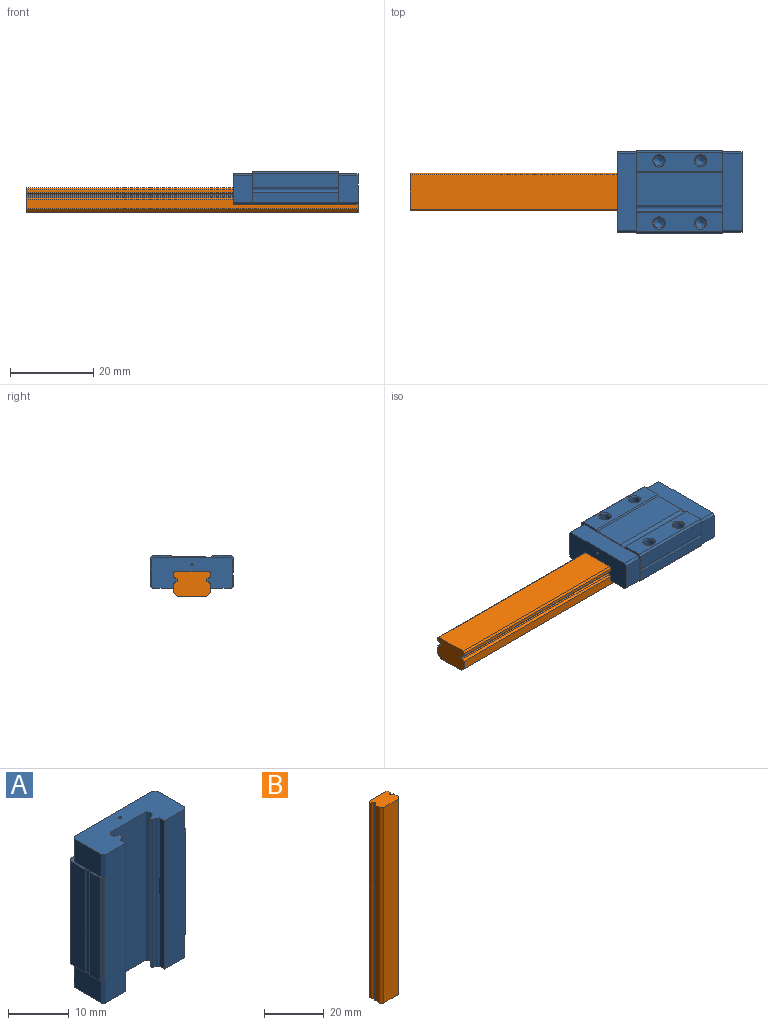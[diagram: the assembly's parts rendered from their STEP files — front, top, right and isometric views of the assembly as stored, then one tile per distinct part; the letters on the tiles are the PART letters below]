
ASSEMBLY  parts=2 mates=1
PART A: 73 faces, bbox 20x8x30 mm
  f0: plane 8x6.01mm, normal (0,0,1), area 5.3mm2, adj f2,f3,f5,f11,f15,f16,f20,f21
  f1: plane 8x6.01mm, normal (0,0,-1), area 5.3mm2, adj f2,f3,f5,f11,f15,f16,f27,f28
  f2: plane 20.8x3.47mm, normal (-1,0,0), area 72.2mm2, adj f0,f1,f16,f72
  f3: plane 20.8x2.47mm, normal (-1,0,0), area 51.4mm2, adj f0,f1,f15,f72
  f4: plane 20.8x4.5mm, normal (0,1,0), area 79.5mm2, adj f6,f7,f12,f38,f44,f68
  f5: plane 20.8x4.5mm, normal (0,1,0), area 79.5mm2, adj f0,f1,f16,f35,f41,f71
  f6: plane 13.99x8mm, normal (0,0,1), area 7.8mm2, adj f4,f10,f12,f13,f14,f17,f18,f19
  f7: plane 13.99x8mm, normal (0,0,-1), area 7.8mm2, adj f4,f10,f12,f13,f14,f24,f25,f26
  f8: plane 19.4x7.4mm, normal (0,0,-1), area 109.2mm2, adj f10,f11,f24,f25,f26,f27,f28,f29
  f9: plane 19.4x7.4mm, normal (0,0,1), area 109.2mm2, adj f10,f11,f17,f18,f19,f20,f21,f22
  f10: plane 30x5mm, normal (0,-1,0), area 147.2mm2, adj f6,f7,f8,f9,f14,f19,f26,f47
  f11: plane 30x5mm, normal (0,-1,0), area 147.2mm2, adj f0,f1,f8,f9,f15,f20,f27,f48
  f12: plane 20.8x0.5mm, normal (0.71,0.71,0), area 14.7mm2, adj f4,f6,f7,f13
  f13: plane 20.8x7mm, normal (1,0,0), area 145.6mm2, adj f6,f7,f12,f14
  f14: plane 20.8x0.5mm, normal (0.71,-0.71,0), area 14.7mm2, adj f6,f7,f10,f13
  f15: plane 20.8x0.5mm, normal (-0.71,-0.71,0), area 14.7mm2, adj f0,f1,f3,f11
  f16: plane 20.8x0.5mm, normal (-0.71,0.71,0), area 14.7mm2, adj f0,f1,f2,f5
  f17: plane 4.6x0.5mm, normal (0.71,0.71,0), area 3.3mm2, adj f6,f9,f18,f23
  f18: plane 6.4x4.6mm, normal (1,0,0), area 29.4mm2, adj f6,f9,f17,f19
  f19: plane 4.6x0.5mm, normal (0.71,-0.71,0), area 3.3mm2, adj f6,f9,f10,f18
  f20: plane 4.6x0.5mm, normal (-0.71,-0.71,0), area 3.3mm2, adj f0,f9,f11,f21
  f21: plane 6.4x4.6mm, normal (-1,0,0), area 29.4mm2, adj f0,f9,f20,f22
  f22: plane 4.6x0.5mm, normal (-0.71,0.71,0), area 3.3mm2, adj f0,f9,f21,f23
  f23: plane 18.4x4.6mm, normal (0,1,0), area 84.6mm2, adj f0,f6,f9,f17,f22
  f24: plane 4.6x0.5mm, normal (0.71,0.71,0), area 3.3mm2, adj f7,f8,f25,f30
  f25: plane 6.4x4.6mm, normal (1,0,0), area 29.4mm2, adj f7,f8,f24,f26
  f26: plane 4.6x0.5mm, normal (0.71,-0.71,0), area 3.3mm2, adj f7,f8,f10,f25
  f27: plane 4.6x0.5mm, normal (-0.71,-0.71,0), area 3.3mm2, adj f1,f8,f11,f28
  f28: plane 6.4x4.6mm, normal (-1,0,0), area 29.4mm2, adj f1,f8,f27,f29
  f29: plane 4.6x0.5mm, normal (-0.71,0.71,0), area 3.3mm2, adj f1,f8,f28,f30
  f30: plane 18.4x4.6mm, normal (0,1,0), area 84.6mm2, adj f1,f7,f8,f24,f29
  f31: cylinder r=0.25mm len=4.6mm, axis (0,0,1), area 7.2mm2, adj f9,f32
  f32: plane 0.5x0.5mm, normal (0,0,1), area 0.2mm2, adj f31
  f33: cylinder r=0.25mm len=4.6mm, axis (0,0,1), area 7.2mm2, adj f8,f34
  f34: plane 0.5x0.5mm, normal (0,0,-1), area 0.2mm2, adj f33
  f35: cone r=1.23mm half-angle=45deg, axis (0,1,0), area 3.3mm2, adj f5,f36
  f36: cylinder r=1.23mm len=3.77mm, axis (0,1,0), area 29.1mm2, adj f35,f37
  f37: cone r=0mm half-angle=60deg, axis (0,1,0), area 5.5mm2, adj f36
  f38: cone r=1.23mm half-angle=45deg, axis (0,1,0), area 3.3mm2, adj f4,f39
  f39: cylinder r=1.23mm len=3.77mm, axis (0,1,0), area 29.1mm2, adj f38,f40
  f40: cone r=0mm half-angle=60deg, axis (0,1,0), area 5.5mm2, adj f39
  f41: cone r=1.23mm half-angle=45deg, axis (0,1,0), area 3.3mm2, adj f5,f42
  f42: cylinder r=1.23mm len=3.77mm, axis (0,1,0), area 29.1mm2, adj f41,f43
  f43: cone r=0mm half-angle=60deg, axis (0,1,0), area 5.5mm2, adj f42
  f44: cone r=1.23mm half-angle=45deg, axis (0,1,0), area 3.3mm2, adj f4,f45
  f45: cylinder r=1.23mm len=3.77mm, axis (0,1,0), area 29.1mm2, adj f44,f46
  f46: cone r=0mm half-angle=60deg, axis (0,1,0), area 5.5mm2, adj f45
  f47: plane 30x1.22mm, normal (-1,0,0), area 36.7mm2, adj f8,f9,f10,f67
  f48: plane 30x1.22mm, normal (1,0,0), area 36.7mm2, adj f8,f9,f11,f49
  f49: cylinder r=0.79mm len=30mm, axis (0,0,1), area 20.2mm2, adj f8,f9,f48,f50
  f50: plane 30x0.45mm, normal (0.17,-0.98,0), area 13.6mm2, adj f8,f9,f49,f51
  f51: cylinder r=0.4mm len=30mm, axis (0,0,1), area 5.8mm2, adj f8,f9,f50,f52
  f52: plane 30x0.35mm, normal (1,0,0), area 10.4mm2, adj f8,f9,f51,f53
  f53: cylinder r=0.4mm len=30mm, axis (0,0,1), area 5.8mm2, adj f8,f9,f52,f54
  f54: plane 30x0.45mm, normal (0.17,0.98,0), area 13.6mm2, adj f8,f9,f53,f55
  f55: cylinder r=0.79mm len=30mm, axis (0,0,1), area 20.2mm2, adj f8,f9,f54,f56
  f56: plane 30x0.72mm, normal (1,0,0), area 21.7mm2, adj f8,f9,f55,f57
  f57: cylinder r=1mm len=30mm, axis (0,0,1), area 19.6mm2, adj f8,f9,f56,f58
  f58: plane 30x8.2mm, normal (0,-1,0), area 246mm2, adj f8,f9,f57,f59
  f59: cylinder r=1mm len=30mm, axis (0,0,1), area 19.6mm2, adj f8,f9,f58,f60
  f60: plane 30x0.72mm, normal (-1,0,0), area 21.7mm2, adj f8,f9,f59,f61
  f61: cylinder r=0.79mm len=30mm, axis (0,0,1), area 20.2mm2, adj f8,f9,f60,f62
  f62: plane 30x0.45mm, normal (-0.17,0.98,0), area 13.6mm2, adj f8,f9,f61,f63
  f63: cylinder r=0.4mm len=30mm, axis (0,0,1), area 5.8mm2, adj f8,f9,f62,f64
  f64: plane 30x0.35mm, normal (-1,0,0), area 10.4mm2, adj f8,f9,f63,f65
  f65: cylinder r=0.4mm len=30mm, axis (0,0,1), area 5.8mm2, adj f8,f9,f64,f66
  f66: plane 30x0.45mm, normal (-0.17,-0.98,0), area 13.6mm2, adj f8,f9,f65,f67
  f67: cylinder r=0.79mm len=30mm, axis (0,0,1), area 20.2mm2, adj f8,f9,f47,f66
  f68: plane 20.8x0.3mm, normal (-0.71,0.71,0), area 8.8mm2, adj f4,f6,f7,f69
  f69: plane 20.8x7.97mm, normal (0,1,0), area 165.8mm2, adj f6,f7,f68,f70
  f70: cylinder r=1mm len=20.8mm, axis (0,0,1), area 33.1mm2, adj f0,f1,f6,f7,f69,f71
  f71: plane 20.8x0.3mm, normal (0.71,0.71,0), area 8.8mm2, adj f0,f1,f5,f70
  f72: cylinder r=0.8mm len=20.8mm, axis (0,0,1), area 24.1mm2, adj f0,f1,f2,f3
PART B: 26 faces, bbox 9x6x80 mm
  f0: plane 80x7mm, normal (0,-1,0), area 560mm2, adj f22,f23,f24,f25
  f1: plane 80x2.22mm, normal (1,0,0), area 177.9mm2, adj f2,f22,f23,f24
  f2: cylinder r=0.79mm len=80mm, axis (0,0,-1), area 53.7mm2, adj f1,f3,f22,f23
  f3: plane 80x0.45mm, normal (0.17,0.98,0), area 36.2mm2, adj f2,f4,f22,f23
  f4: cylinder r=0.4mm len=80mm, axis (0,0,-1), area 15.4mm2, adj f3,f5,f22,f23
  f5: plane 80x0.35mm, normal (1,0,0), area 27.8mm2, adj f4,f6,f22,f23
  f6: cylinder r=0.4mm len=80mm, axis (0,0,-1), area 15.4mm2, adj f5,f7,f22,f23
  f7: plane 80x0.45mm, normal (0.17,-0.98,0), area 36.2mm2, adj f6,f8,f22,f23
  f8: cylinder r=0.79mm len=80mm, axis (0,0,-1), area 53.7mm2, adj f7,f9,f22,f23
  f9: plane 80x0.72mm, normal (1,0,0), area 57.9mm2, adj f8,f10,f22,f23
  f10: cylinder r=1mm len=80mm, axis (0,0,-1), area 52.1mm2, adj f9,f11,f22,f23
  f11: plane 80x8.2mm, normal (0,1,0), area 656mm2, adj f10,f12,f22,f23
  f12: cylinder r=1mm len=80mm, axis (0,0,-1), area 52.1mm2, adj f11,f13,f22,f23
  f13: plane 80x0.72mm, normal (-1,0,0), area 57.9mm2, adj f12,f14,f22,f23
  f14: cylinder r=0.79mm len=80mm, axis (0,0,-1), area 53.7mm2, adj f13,f15,f22,f23
  f15: plane 80x0.45mm, normal (-0.17,-0.98,0), area 36.2mm2, adj f14,f16,f22,f23
  f16: cylinder r=0.4mm len=80mm, axis (0,0,-1), area 15.4mm2, adj f15,f17,f22,f23
  f17: plane 80x0.35mm, normal (-1,0,0), area 27.8mm2, adj f16,f18,f22,f23
  f18: cylinder r=0.4mm len=80mm, axis (0,0,-1), area 15.4mm2, adj f17,f19,f22,f23
  f19: plane 80x0.45mm, normal (-0.17,0.98,0), area 36.2mm2, adj f18,f20,f22,f23
  f20: cylinder r=0.79mm len=80mm, axis (0,0,-1), area 53.7mm2, adj f19,f21,f22,f23
  f21: plane 80x2.22mm, normal (-1,0,0), area 177.9mm2, adj f20,f22,f23,f25
  f22: plane 9x6mm, normal (0,0,1), area 50.7mm2, adj f0,f1,f2,f3,f4,f5,f6,f7
  f23: plane 9x6mm, normal (0,0,-1), area 50.7mm2, adj f0,f1,f2,f3,f4,f5,f6,f7
  f24: plane 80x1mm, normal (0.71,-0.71,0), area 113.1mm2, adj f0,f1,f22,f23
  f25: plane 80x1mm, normal (-0.71,-0.71,0), area 113.1mm2, adj f0,f21,f22,f23
PLACE A rot(axis=(0.58,0.58,0.58),120deg) t=(65,0,0)mm
PLACE B rot(axis=(0.58,0.58,0.58),120deg) t=(-15,0,0)mm
MATE slider B.f23 <-> A.f8  axis (-1,0,0) through (0,0,6)mm
